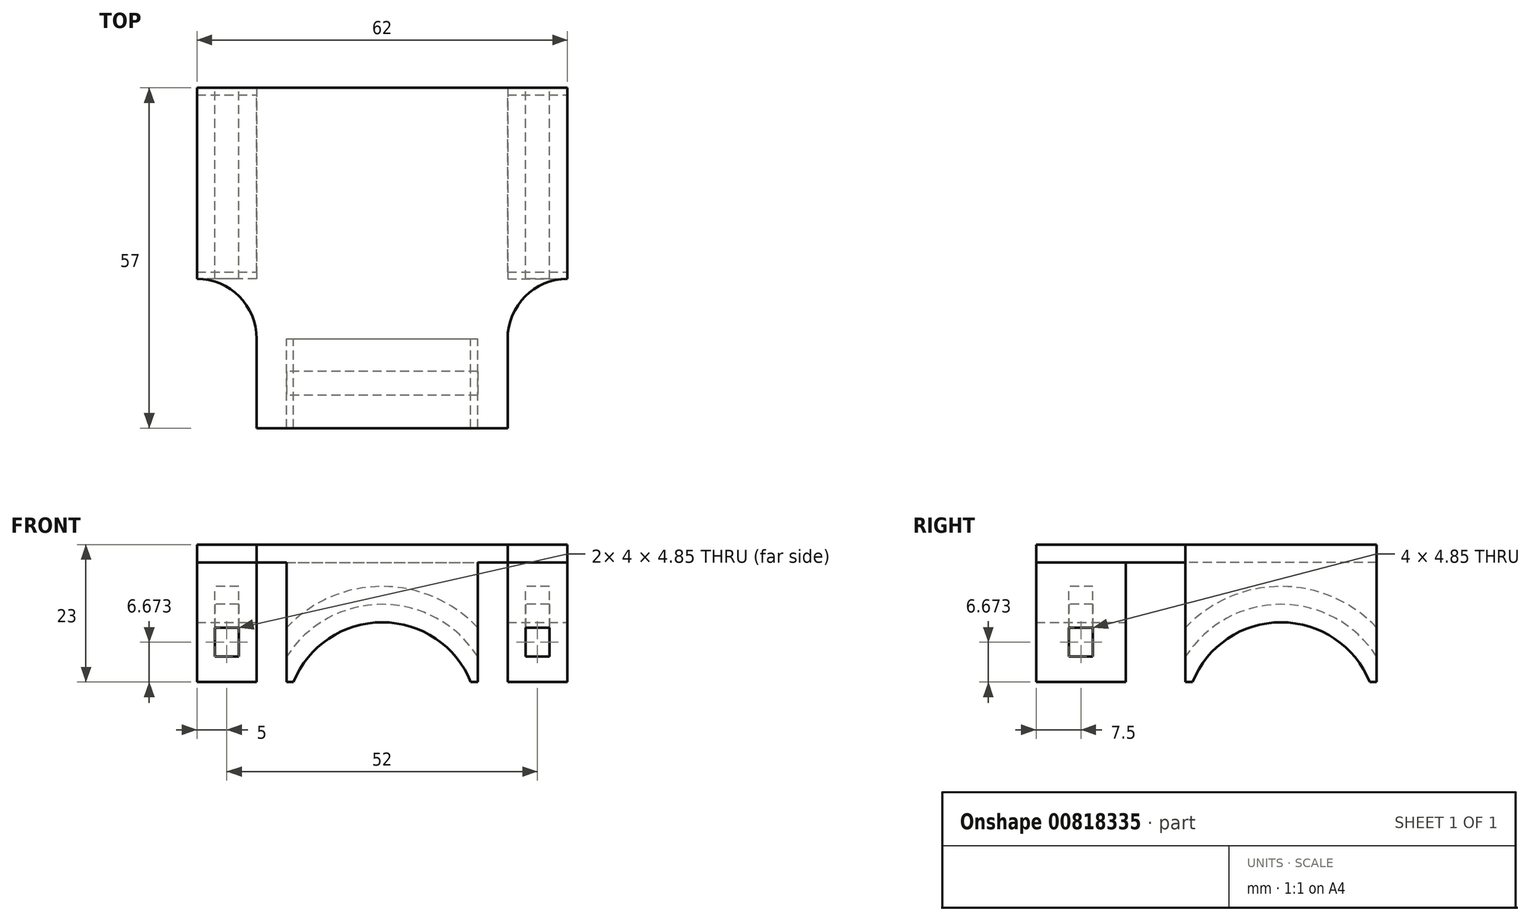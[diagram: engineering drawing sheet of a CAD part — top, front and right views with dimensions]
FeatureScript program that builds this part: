
annotation { "Feature Type Name" : "Feature", "Feature Type Description" : "" }
export const myFeature = defineFeature(function(context is Context, id is Id, definition is map)
    precondition{}
    {
        {
            var Q0;
            Q0=qCreatedBy(makeId("Top.planeOp"),FACE);
            var sketch = newSketch(context, id + "F0", { "sketchPlane" : qUnion([Q0])});
            skLineSegment(sketch, "E0.bottom", {"start": v(0, 0) * mm, "end": v(42, 0) * mm});
            skLineSegment(sketch, "E0.top", {"start": v(0, -57) * mm, "end": v(42, -57) * mm});
            skLineSegment(sketch, "E0.left", {"start": v(0, 0) * mm, "end": v(0, -57) * mm});
            skLineSegment(sketch, "E0.right", {"start": v(42, 0) * mm, "end": v(42, -57) * mm});
            skLineSegment(sketch, "E1.bottom", {"start": v(42, 0) * mm, "end": v(52, 0) * mm});
            skLineSegment(sketch, "E1.top", {"start": v(42, -32) * mm, "end": v(52, -32) * mm});
            skLineSegment(sketch, "E1.left", {"start": v(42, 0) * mm, "end": v(42, -32) * mm});
            skLineSegment(sketch, "E1.right", {"start": v(52, 0) * mm, "end": v(52, -32) * mm});
            skLineSegment(sketch, "E2.bottom", {"start": v(0, 0) * mm, "end": v(-10, 0) * mm});
            skLineSegment(sketch, "E2.top", {"start": v(0, -32) * mm, "end": v(-10, -32) * mm});
            skLineSegment(sketch, "E2.left", {"start": v(0, 0) * mm, "end": v(0, -32) * mm});
            skLineSegment(sketch, "E2.right", {"start": v(-10, 0) * mm, "end": v(-10, -32) * mm});
            skArc(sketch, "E3", {"start": v(0, -42) * mm, "mid": v(-2.93, -34.93) * mm, "end": v(-10, -32) * mm});
            skArc(sketch, "E4", {"start": v(52, -32) * mm, "mid": v(44.93, -34.93) * mm, "end": v(42, -42) * mm});
            skSolve(sketch);
        }
        {
            var Q0;
            Q0=makeQuery(id+"F0.imprint","IMPRINT",FACE,{"disambiguationData":[TD([[makeQuery(id+"F0.imprint","IMPRINT",EDGE,{"derivedFrom":sQuery(id+"F0.wireOp",EDGE,"E0.bottom")}),-1.0]])]});
            extrude(context, id + "F1", {"entities" : qUnion([Q0]), "depth" : -3 * mm, "offsetDistance" : 25 * mm});
        }
        {
            var Q0;
            Q0=makeQuery(id+"F0.imprint","IMPRINT",FACE,{"disambiguationData":[TD([[makeQuery(id+"F0.imprint","IMPRINT",EDGE,{"derivedFrom":sQuery(id+"F0.wireOp",EDGE,"E1.bottom")}),-1.0]])]});
            var Q1;
            Q1=makeQuery(id+"F0.imprint","IMPRINT",FACE,{"disambiguationData":[TD([[makeQuery(id+"F0.imprint","IMPRINT",EDGE,{"derivedFrom":sQuery(id+"F0.wireOp",EDGE,"E2.bottom")}),1.0]])]});
            extrude(context, id + "F2", {"entities" : qUnion([Q0, Q1]), "operationType" : NewBodyOperationType.ADD, "depth" : -13 * mm, "offsetDistance" : 25 * mm});
        }
        {
            var Q0;
            Q0=makeQuery(id+"F2.opExtrude","CAP_FACE",FACE,{"disambiguationData":[OSD([sQuery(id+"F0.wireOp",EDGE,"E1.bottom"),sQuery(id+"F0.wireOp",EDGE,"E1.top"),sQuery(id+"F0.wireOp",EDGE,"E1.left"),sQuery(id+"F0.wireOp",EDGE,"E1.right")])],"isStart":false});
            var Q1;
            Q1=makeQuery(id+"F2.opExtrude","CAP_FACE",FACE,{"disambiguationData":[OSD([sQuery(id+"F0.wireOp",EDGE,"E2.bottom"),sQuery(id+"F0.wireOp",EDGE,"E2.top"),sQuery(id+"F0.wireOp",EDGE,"E2.left"),sQuery(id+"F0.wireOp",EDGE,"E2.right")])],"isStart":false});
            extrude(context, id + "F3", {"entities" : qUnion([Q0, Q1]), "operationType" : NewBodyOperationType.ADD, "depth" : 10 * mm, "offsetDistance" : 25 * mm});
        }
        {
            var Q0;
            {var subQ0=sQuery(id+"F0.wireOp",EDGE,"E1.right");Q0=makeQuery(id+"F3.boolean.opBoolean","MERGE",FACE,{"derivedFrom":[makeQuery(id+"F2.opExtrude","SWEPT_FACE",FACE,{"disambiguationData":[OSD([subQ0])]}),makeQuery(id+"F3.opExtrude","SWEPT_FACE",FACE,{"disambiguationData":[OSD([subQ0])]})]});}
            var sketch = newSketch(context, id + "F4", { "sketchPlane" : qUnion([Q0])});
            skCircle(sketch, "E5", {"center": v(-16, -29) * mm, "radius": 16 * mm});
            skSolve(sketch);
        }
        {
            var Q0;
            Q0 = qSketchRegion(id + "F4", true);
            extrude(context, id + "F5", {"entities" : qUnion([Q0]), "operationType" : NewBodyOperationType.REMOVE, "endBound" : BoundingType.THROUGH_ALL, "oppositeDirection" : true, "depth" : 25 * mm, "offsetDistance" : 25 * mm});
        }
        {
            var Q0;
            Q0=makeQuery(id+"F0.imprint","IMPRINT",FACE,{"disambiguationData":[TD([[makeQuery(id+"F0.imprint","IMPRINT",EDGE,{"derivedFrom":sQuery(id+"F0.wireOp",EDGE,"E0.bottom")}),-1.0]])]});
            var sketch = newSketch(context, id + "F6", { "sketchPlane" : qUnion([Q0])});
            skLineSegment(sketch, "E6.bottom", {"start": v(5, -57) * mm, "end": v(37, -57) * mm});
            skLineSegment(sketch, "E6.top", {"start": v(5, -42) * mm, "end": v(37, -42) * mm});
            skLineSegment(sketch, "E6.left", {"start": v(5, -57) * mm, "end": v(5, -42) * mm});
            skLineSegment(sketch, "E6.right", {"start": v(37, -57) * mm, "end": v(37, -42) * mm});
            skSolve(sketch);
        }
        {
            var Q0;
            Q0 = qSketchRegion(id + "F6", true);
            extrude(context, id + "F7", {"entities" : qUnion([Q0]), "operationType" : NewBodyOperationType.ADD, "depth" : -23 * mm, "offsetDistance" : 25 * mm});
        }
        {
            var Q0;
            Q0=makeQuery(id+"F7.opExtrude","SWEPT_FACE",FACE,{"disambiguationData":[OSD([sQuery(id+"F6.wireOp",EDGE,"E6.top")])]});
            var sketch = newSketch(context, id + "F8", { "sketchPlane" : qUnion([Q0])});
            skCircle(sketch, "E7", {"center": v(-21, -29) * mm, "radius": 16 * mm});
            skSolve(sketch);
        }
        {
            var Q0;
            Q0 = qSketchRegion(id + "F8", true);
            extrude(context, id + "F9", {"entities" : qUnion([Q0]), "operationType" : NewBodyOperationType.REMOVE, "endBound" : BoundingType.THROUGH_ALL, "oppositeDirection" : true, "depth" : 25 * mm, "offsetDistance" : 25 * mm});
        }
        {
            var Q0;
            {var subQ0=sQuery(id+"F0.wireOp",EDGE,"E2.right");Q0=makeQuery(id+"F3.boolean.opBoolean","MERGE",FACE,{"derivedFrom":[makeQuery(id+"F2.opExtrude","SWEPT_FACE",FACE,{"disambiguationData":[OSD([subQ0])]}),makeQuery(id+"F3.opExtrude","SWEPT_FACE",FACE,{"disambiguationData":[OSD([subQ0])]})]});}
            var sketch = newSketch(context, id + "F10", { "sketchPlane" : qUnion([Q0])});
            skCircle(sketch, "E8", {"center": v(16, -29) * mm, "radius": 19 * mm});
            skCircle(sketch, "E9", {"center": v(16, -29) * mm, "radius": 22 * mm});
            skSolve(sketch);
        }
        {
            var Q0;
            {var subQ0=sQuery(id+"F10.wireOp",EDGE,"E8");var subQ1=sQuery(id+"F0.wireOp",EDGE,"E2.right");var subQ2=sQuery(id+"F0.wireOp",EDGE,"E2.bottom");var subQ3=makeQuery(id+"F3.boolean.opBoolean","MERGE",EDGE,{"derivedFrom":[makeQuery(id+"F2.opExtrude","SWEPT_EDGE",EDGE,{"disambiguationData":[OSD([subQ2,subQ1])]}),makeQuery(id+"F3.opExtrude","SWEPT_EDGE",EDGE,{"disambiguationData":[OSD([subQ2,subQ1])]})]});var subQ4=makeQuery(id+"F10.imprint","INTERSECT",VERTEX,{"derivedFrom":[subQ3,subQ0]});Q0=makeQuery(id+"F10.imprint","IMPRINT",FACE,{"disambiguationData":[TD([[makeQuery(id+"F10.imprint","IMPRINT",EDGE,{"disambiguationData":[TD([[subQ4,1.0]])],"derivedFrom":subQ0}),-1.0]])]});}
            extrude(context, id + "F11", {"entities" : qUnion([Q0]), "operationType" : NewBodyOperationType.REMOVE, "oppositeDirection" : true, "depth" : 7 * mm, "offsetDistance" : 25 * mm, "hasSecondDirection" : true, "secondDirectionOppositeDirection" : true, "secondDirectionDepth" : 3 * mm});
        }
        {
            var Q0;
            {var subQ0=sQuery(id+"F10.wireOp",EDGE,"E8");var subQ1=sQuery(id+"F0.wireOp",EDGE,"E2.right");var subQ2=sQuery(id+"F0.wireOp",EDGE,"E2.bottom");var subQ3=makeQuery(id+"F3.boolean.opBoolean","MERGE",EDGE,{"derivedFrom":[makeQuery(id+"F2.opExtrude","SWEPT_EDGE",EDGE,{"disambiguationData":[OSD([subQ2,subQ1])]}),makeQuery(id+"F3.opExtrude","SWEPT_EDGE",EDGE,{"disambiguationData":[OSD([subQ2,subQ1])]})]});var subQ4=makeQuery(id+"F10.imprint","INTERSECT",VERTEX,{"derivedFrom":[subQ3,subQ0]});Q0=makeQuery(id+"F10.imprint","IMPRINT",FACE,{"disambiguationData":[TD([[makeQuery(id+"F10.imprint","IMPRINT",EDGE,{"disambiguationData":[TD([[subQ4,1.0]])],"derivedFrom":subQ0}),-1.0]])]});}
            extrude(context, id + "F12", {"entities" : qUnion([Q0]), "operationType" : NewBodyOperationType.REMOVE, "oppositeDirection" : true, "depth" : 59 * mm, "offsetDistance" : 25 * mm, "hasSecondDirection" : true, "secondDirectionOppositeDirection" : true, "secondDirectionDepth" : 55 * mm});
        }
        {
            var Q0;
            Q0=makeQuery(id+"F7.boolean.opBoolean","MERGE",FACE,{"derivedFrom":[makeQuery(id+"F1.opExtrude","SWEPT_FACE",FACE,{"disambiguationData":[OSD([sQuery(id+"F0.wireOp",EDGE,"E0.top")])]}),makeQuery(id+"F7.opExtrude","SWEPT_FACE",FACE,{"disambiguationData":[OSD([sQuery(id+"F6.wireOp",EDGE,"E6.bottom")])]})]});
            var sketch = newSketch(context, id + "F13", { "sketchPlane" : qUnion([Q0])});
            skCircle(sketch, "E10", {"center": v(21, -29) * mm, "radius": 19 * mm});
            skCircle(sketch, "E11", {"center": v(21, -29) * mm, "radius": 22 * mm});
            skSolve(sketch);
        }
        {
            var Q0;
            {var subQ0=sQuery(id+"F13.wireOp",EDGE,"E10");var subQ1=sQuery(id+"F6.wireOp",EDGE,"E6.bottom");var subQ2=sQuery(id+"F0.wireOp",EDGE,"E0.top");var subQ3=makeQuery(id+"F7.opExtrude","SWEPT_EDGE",EDGE,{"disambiguationData":[OSD([subQ2,subQ1,sQuery(id+"F6.wireOp",EDGE,"E6.left")])]});var subQ4=makeQuery(id+"F13.imprint","INTERSECT",VERTEX,{"derivedFrom":[subQ3,subQ0]});Q0=makeQuery(id+"F13.imprint","IMPRINT",FACE,{"disambiguationData":[TD([[makeQuery(id+"F13.imprint","IMPRINT",EDGE,{"disambiguationData":[TD([[subQ4,1.0]])],"derivedFrom":subQ0}),-1.0]])]});}
            extrude(context, id + "F14", {"entities" : qUnion([Q0]), "operationType" : NewBodyOperationType.REMOVE, "oppositeDirection" : true, "depth" : 9.5 * mm, "offsetDistance" : 25 * mm, "hasSecondDirection" : true, "secondDirectionOppositeDirection" : true, "secondDirectionDepth" : 5.5 * mm});
        }
        {
            var Q0;
            {var subQ0=sQuery(id+"F0.wireOp",EDGE,"E1.top");Q0=makeQuery(id+"F0.imprint","IMPRINT",FACE,{"disambiguationData":[TD([[makeQuery(id+"F0.imprint","IMPRINT",EDGE,{"derivedFrom":subQ0}),-1.0]])]});}
            var Q1;
            {var subQ0=sQuery(id+"F0.wireOp",EDGE,"E2.top");Q1=makeQuery(id+"F0.imprint","IMPRINT",FACE,{"disambiguationData":[TD([[makeQuery(id+"F0.imprint","IMPRINT",EDGE,{"derivedFrom":subQ0}),1.0]])]});}
            extrude(context, id + "F15", {"entities" : qUnion([Q0, Q1]), "operationType" : NewBodyOperationType.ADD, "depth" : -3 * mm, "offsetDistance" : 25 * mm});
        }
    });
